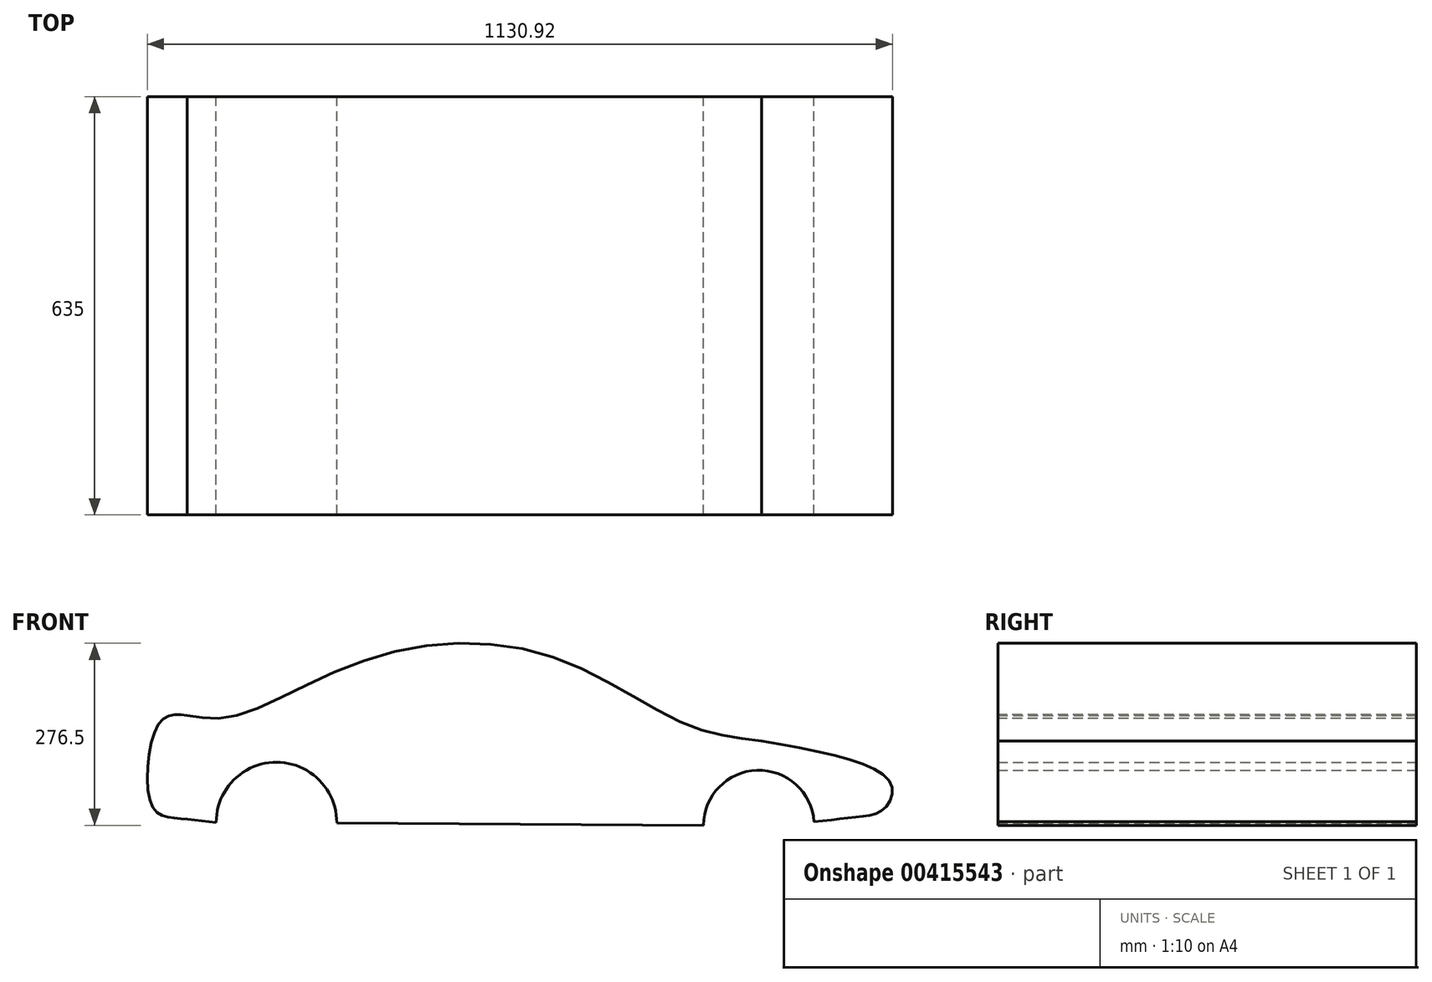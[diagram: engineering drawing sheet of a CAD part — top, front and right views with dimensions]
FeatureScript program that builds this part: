
annotation { "Feature Type Name" : "Feature", "Feature Type Description" : "" }
export const myFeature = defineFeature(function(context is Context, id is Id, definition is map)
    precondition{}
    {
        {
            var Q0;
            Q0=qCreatedBy(makeId("Front.planeOp"),FACE);
            var sketch = newSketch(context, id + "F0", { "sketchPlane" : qUnion([Q0])});
            skLineSegment(sketch, "E0", {"start": v(-109.87, 29.88) * mm, "end": v(-666.32, 33.51) * mm});
            skArc(sketch, "E1", {"start": v(-666.32, 33.51) * mm, "mid": v(-757.57, 125.66) * mm, "end": v(-849.41, 34.11) * mm});
            skFitSpline(sketch, "E2", {"points": [v(-849.41, 34.11) * mm, v(-908.65, 40.46) * mm, v(-946.6, 59.08) * mm, v(-934.8, 186.27) * mm, v(-893.35, 196.63) * mm], "startDerivative": vector(-253.15, 28.99) * mm, "endDerivative": vector(224.03, -29.85) * mm});
            skFitSpline(sketch, "E3", {"points": [v(-893.35, 196.63) * mm, v(-817.85, 196.63) * mm, v(-617.98, 282.5) * mm, v(-342.6, 286.94) * mm, v(-139.78, 184.79) * mm, v(-21.34, 158.14) * mm], "startDerivative": vector(522.33, -88.46) * mm, "endDerivative": vector(683.74, -75.01) * mm});
            skArc(sketch, "E4", {"start": v(58.1, 35.24) * mm, "mid": v(-28.46, 113.38) * mm, "end": v(-109.87, 29.88) * mm});
            skFitSpline(sketch, "E5", {"points": [v(58.1, 35.24) * mm, v(125.23, 42.66) * mm, v(163.72, 54.5) * mm, v(174.09, 94.48) * mm, v(-21.34, 158.14) * mm], "startDerivative": vector(305.23, 34.39) * mm, "endDerivative": vector(-662, 120.22) * mm});
            skSolve(sketch);
        }
        {
            var Q0;
            Q0=makeQuery(id+"F0.imprint","IMPRINT",FACE,{"disambiguationData":[TD([[makeQuery(id+"F0.imprint","IMPRINT",EDGE,{"derivedFrom":sQuery(id+"F0.wireOp",EDGE,"E0")}),-1.0]])]});
            extrude(context, id + "F1", {"entities" : qUnion([Q0]), "depth" : 635 * mm, "offsetDistance" : 25.4 * mm});
        }
    });
